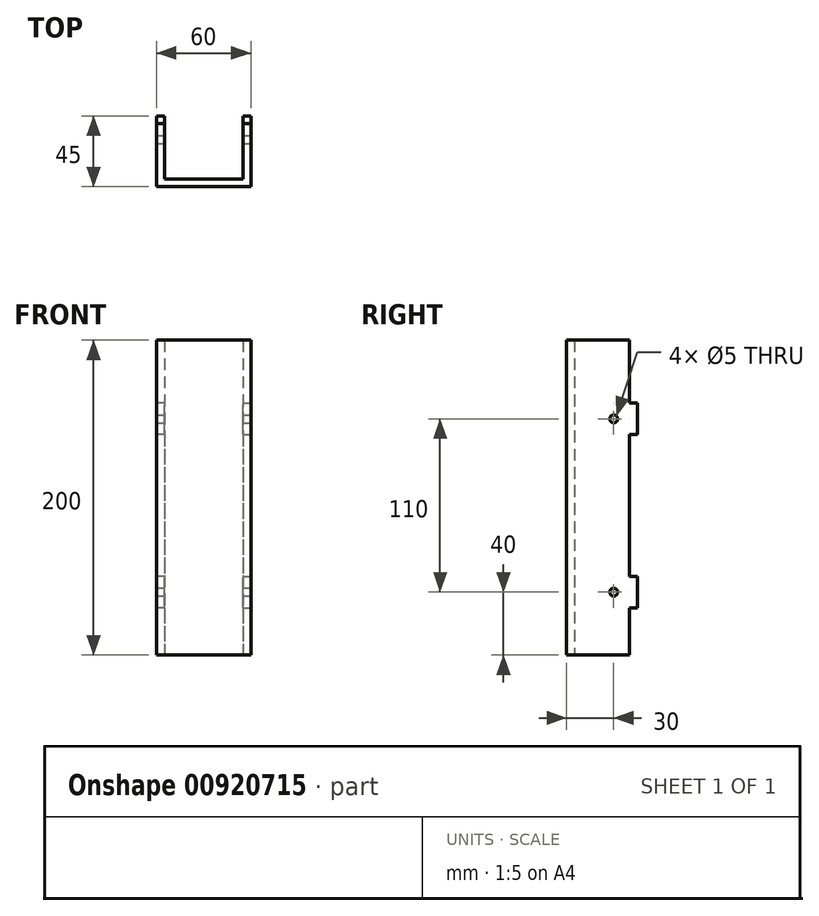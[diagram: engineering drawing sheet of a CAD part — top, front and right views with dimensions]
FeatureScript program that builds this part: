
annotation { "Feature Type Name" : "Feature", "Feature Type Description" : "" }
export const myFeature = defineFeature(function(context is Context, id is Id, definition is map)
    precondition{}
    {
        {
            assignVariable(context, id + "F0", {"variableType" : VariableType.LENGTH, "name" : "podlength", "lengthValue" : 200 * mm});
        }
        {
            var Q0;
            Q0=qCreatedBy(makeId("Top.planeOp"),FACE);
            var sketch = newSketch(context, id + "F1", { "sketchPlane" : qUnion([Q0])});
            skLineSegment(sketch, "E0.bottom", {"start": v(65, 0) * mm, "end": v(30, 0) * mm});
            skLineSegment(sketch, "E0.top", {"start": v(65, 200) * mm, "end": v(30, 200) * mm});
            skLineSegment(sketch, "E0.right", {"start": v(-65, 0) * mm, "end": v(-65, 200) * mm});
            skPoint(sketch, "E1", {"position": v(0, 0) * mm});
            skLineSegment(sketch, "E2", {"start": v(25, 200) * mm, "end": v(25, 0) * mm});
            skLineSegment(sketch, "E3", {"start": v(-25, 200) * mm, "end": v(-25, 0) * mm});
            skLineSegment(sketch, "E4", {"start": v(-30, 200) * mm, "end": v(-30, 0) * mm});
            skLineSegment(sketch, "E5", {"start": v(30, 200) * mm, "end": v(30, 0) * mm});
            skLineSegment(sketch, "E6", {"start": v(65, 200) * mm, "end": v(65, 0) * mm});
            skLineSegment(sketch, "E7.0", {"start": v(-35, 200) * mm, "end": v(-35, 0) * mm, "construction": true});
            skLineSegment(sketch, "E8.0", {"start": v(35, 200) * mm, "end": v(35, 0) * mm, "construction": true});
            skLineSegment(sketch, "E9.bottom", {"start": v(30, -15) * mm, "end": v(-30, -15) * mm});
            skLineSegment(sketch, "E9.top", {"start": v(30, -55) * mm, "end": v(-30, -55) * mm});
            skLineSegment(sketch, "E9.left", {"start": v(30, -15) * mm, "end": v(30, -55) * mm});
            skLineSegment(sketch, "E9.right", {"start": v(-30, -15) * mm, "end": v(-30, -55) * mm});
            skLineSegment(sketch, "E10.0", {"start": v(-25, -15) * mm, "end": v(-25, -50) * mm});
            skLineSegment(sketch, "E10.1", {"start": v(25, -50) * mm, "end": v(-25, -50) * mm});
            skLineSegment(sketch, "E10.2", {"start": v(25, -15) * mm, "end": v(25, -50) * mm});
            skLineSegment(sketch, "E11", {"start": v(-65, 30) * mm, "end": v(-70, 30) * mm});
            skLineSegment(sketch, "E12", {"start": v(-70, 30) * mm, "end": v(-70, 50) * mm});
            skLineSegment(sketch, "E13", {"start": v(-70, 50) * mm, "end": v(-65, 50) * mm});
            skLineSegment(sketch, "E14", {"start": v(65, 30) * mm, "end": v(70, 30) * mm});
            skLineSegment(sketch, "E15", {"start": v(70, 30) * mm, "end": v(70, 50) * mm});
            skLineSegment(sketch, "E16", {"start": v(70, 50) * mm, "end": v(65, 50) * mm});
            skLineSegment(sketch, "E17", {"start": v(65, 140) * mm, "end": v(70, 140) * mm});
            skLineSegment(sketch, "E18", {"start": v(70, 140) * mm, "end": v(70, 160) * mm});
            skLineSegment(sketch, "E19", {"start": v(70, 160) * mm, "end": v(65, 160) * mm});
            skLineSegment(sketch, "E20", {"start": v(-65, 140) * mm, "end": v(-70, 140) * mm});
            skLineSegment(sketch, "E21", {"start": v(-70, 140) * mm, "end": v(-70, 160) * mm});
            skLineSegment(sketch, "E22", {"start": v(-70, 160) * mm, "end": v(-65, 160) * mm});
            skPoint(sketch, "E23", {"position": v(-55, 40) * mm});
            skPoint(sketch, "E23.positionSnap0", {"position": v(-70, 40) * mm});
            skPoint(sketch, "E24", {"position": v(55, 40) * mm});
            skPoint(sketch, "E24.positionSnap0", {"position": v(70, 40) * mm});
            skPoint(sketch, "E25", {"position": v(55, 150) * mm});
            skPoint(sketch, "E25.positionSnap0", {"position": v(70, 150) * mm});
            skPoint(sketch, "E26", {"position": v(-55, 150) * mm});
            skPoint(sketch, "E26.positionSnap0", {"position": v(-70, 150) * mm});
            skCircle(sketch, "E27", {"center": v(-55, 150) * mm, "radius": 2.5 * mm});
            skCircle(sketch, "E28", {"center": v(55, 150) * mm, "radius": 2.5 * mm});
            skCircle(sketch, "E29", {"center": v(-55, 40) * mm, "radius": 2.5 * mm});
            skCircle(sketch, "E30", {"center": v(55, 40) * mm, "radius": 2.5 * mm});
            skPoint(sketch, "E31", {"position": v(0, -55) * mm});
            skLineSegment(sketch, "E32.trimOffspring", {"start": v(-30, 200) * mm, "end": v(-65, 200) * mm});
            skLineSegment(sketch, "E33.trimOffspring", {"start": v(25, 200) * mm, "end": v(-25, 200) * mm});
            skLineSegment(sketch, "E34.trimOffspring", {"start": v(25, 0) * mm, "end": v(-25, 0) * mm});
            skLineSegment(sketch, "E35.trimOffspring", {"start": v(-30, 0) * mm, "end": v(-65, 0) * mm});
            skLineSegment(sketch, "E36", {"start": v(-25, -50) * mm, "end": v(-25, -55) * mm, "construction": true});
            skLineSegment(sketch, "E37", {"start": v(25, -50) * mm, "end": v(25, -55) * mm, "construction": true});
            skSolve(sketch);
        }
        {
            var Q0;
            Q0=makeQuery(id+"F1.imprint","IMPRINT",FACE,{"disambiguationData":[TD([[makeQuery(id+"F1.imprint","IMPRINT",EDGE,{"derivedFrom":sQuery(id+"F1.wireOp",EDGE,"E9.top")}),-1.0]])]});
            extrude(context, id + "F2", {"entities" : qUnion([Q0]), "depth" : getVariable(context, 'podlength'), "offsetDistance" : 25 * mm});
        }
        {
            var Q0;
            Q0=makeQuery(id+"F2.opExtrude","SWEPT_FACE",FACE,{"disambiguationData":[OSD([sQuery(id+"F1.wireOp",EDGE,"E9.left")])]});
            var sketch = newSketch(context, id + "F3", { "sketchPlane" : qUnion([Q0])});
            skLineSegment(sketch, "E38.0.0", {"start": v(-55, 0) * mm, "end": v(-15, 0) * mm});
            skLineSegment(sketch, "E38.0.1", {"start": v(-15, 0) * mm, "end": v(-15, 200) * mm});
            skLineSegment(sketch, "E38.0.2", {"start": v(-15, 200) * mm, "end": v(-55, 200) * mm});
            skLineSegment(sketch, "E38.0.3", {"start": v(-55, 200) * mm, "end": v(-55, 0) * mm});
            skLineSegment(sketch, "E39", {"start": v(-15, 30) * mm, "end": v(-10, 30) * mm});
            skLineSegment(sketch, "E40", {"start": v(-10, 30) * mm, "end": v(-10, 50) * mm});
            skLineSegment(sketch, "E41", {"start": v(-10, 50) * mm, "end": v(-15, 50) * mm});
            skLineSegment(sketch, "E42", {"start": v(-15, 140) * mm, "end": v(-10, 140) * mm});
            skLineSegment(sketch, "E43", {"start": v(-10, 140) * mm, "end": v(-10, 160) * mm});
            skLineSegment(sketch, "E44", {"start": v(-10, 160) * mm, "end": v(-15, 160) * mm});
            skPoint(sketch, "E45", {"position": v(-25, 150) * mm});
            skPoint(sketch, "E45.positionSnap0", {"position": v(-10, 150) * mm});
            skPoint(sketch, "E46", {"position": v(-10, 40) * mm});
            skPoint(sketch, "E47", {"position": v(-25, 40) * mm});
            skSolve(sketch);
        }
        {
            var Q0;
            {var subQ0=sQuery(id+"F3.wireOp",EDGE,"E42");Q0=makeQuery(id+"F3.imprint","IMPRINT",FACE,{"disambiguationData":[TD([[makeQuery(id+"F3.imprint","IMPRINT",EDGE,{"derivedFrom":subQ0}),1.0]])]});}
            var Q1;
            {var subQ0=sQuery(id+"F3.wireOp",EDGE,"E39");Q1=makeQuery(id+"F3.imprint","IMPRINT",FACE,{"disambiguationData":[TD([[makeQuery(id+"F3.imprint","IMPRINT",EDGE,{"derivedFrom":subQ0}),1.0]])]});}
            extrude(context, id + "F4", {"entities" : qUnion([Q0, Q1]), "operationType" : NewBodyOperationType.ADD, "oppositeDirection" : true, "depth" : 5 * mm, "offsetDistance" : 25 * mm});
        }
        {
            var Q0;
            Q0=makeQuery(id+"F2.opExtrude","SWEPT_FACE",FACE,{"disambiguationData":[OSD([sQuery(id+"F1.wireOp",EDGE,"E9.right")])]});
            var sketch = newSketch(context, id + "F5", { "sketchPlane" : qUnion([Q0])});
            skLineSegment(sketch, "E48.0.0", {"start": v(15, 0) * mm, "end": v(55, 0) * mm});
            skLineSegment(sketch, "E48.0.1", {"start": v(55, 0) * mm, "end": v(55, 200) * mm});
            skLineSegment(sketch, "E48.0.2", {"start": v(55, 200) * mm, "end": v(15, 200) * mm});
            skLineSegment(sketch, "E48.0.3", {"start": v(15, 200) * mm, "end": v(15, 0) * mm});
            skLineSegment(sketch, "E49.0.0", {"start": v(10, 140) * mm, "end": v(10, 160) * mm});
            skLineSegment(sketch, "E49.0.1", {"start": v(10, 160) * mm, "end": v(15, 160) * mm});
            skLineSegment(sketch, "E49.0.2", {"start": v(15, 160) * mm, "end": v(15, 140) * mm});
            skLineSegment(sketch, "E49.0.3", {"start": v(15, 140) * mm, "end": v(10, 140) * mm});
            skLineSegment(sketch, "E50.0.0", {"start": v(10, 30) * mm, "end": v(10, 50) * mm});
            skLineSegment(sketch, "E50.0.1", {"start": v(10, 50) * mm, "end": v(15, 50) * mm});
            skLineSegment(sketch, "E50.0.2", {"start": v(15, 50) * mm, "end": v(15, 30) * mm});
            skLineSegment(sketch, "E50.0.3", {"start": v(15, 30) * mm, "end": v(10, 30) * mm});
            skSolve(sketch);
        }
        {
            var Q0;
            Q0=makeQuery(id+"F5.imprint","IMPRINT",FACE,{"disambiguationData":[TD([[makeQuery(id+"F5.imprint","IMPRINT",EDGE,{"derivedFrom":sQuery(id+"F5.wireOp",EDGE,"E49.0.0")}),-1.0]])]});
            var Q1;
            Q1=makeQuery(id+"F5.imprint","IMPRINT",FACE,{"disambiguationData":[TD([[makeQuery(id+"F5.imprint","IMPRINT",EDGE,{"derivedFrom":sQuery(id+"F5.wireOp",EDGE,"E50.0.0")}),-1.0]])]});
            extrude(context, id + "F6", {"entities" : qUnion([Q0, Q1]), "operationType" : NewBodyOperationType.ADD, "oppositeDirection" : true, "depth" : 5 * mm, "offsetDistance" : 25 * mm});
        }
        {
            var Q0;
            Q0=sQuery(id+"F3.wireOp",VERTEX,"E45");
            var Q1;
            Q1=sQuery(id+"F3.wireOp",VERTEX,"E47");
            var Q2;
            Q2=makeQuery(id+"F2.opExtrude","SWEPT_BODY",BODY,{"disambiguationData":[OSD([sQuery(id+"F1.wireOp",EDGE,"E9.bottom"),sQuery(id+"F1.wireOp",EDGE,"E9.top"),sQuery(id+"F1.wireOp",EDGE,"E9.left"),sQuery(id+"F1.wireOp",EDGE,"E9.right"),sQuery(id+"F1.wireOp",EDGE,"E10.0"),sQuery(id+"F1.wireOp",EDGE,"E10.1"),sQuery(id+"F1.wireOp",EDGE,"E10.2")])]});
            hole(context, id + "F7", {"style" : HoleStyle.SIMPLE, "endStyle" : HoleEndStyle.THROUGH, "holeDiameter" : 5 * mm, "majorDiameter" : 5 * mm, "isTappedThrough" : true, "tappedDepth" : 12 * mm, "tapClearance" : 3, "locations" : qUnion([Q0, Q1]), "scope" : qUnion([Q2])});
        }
    });
